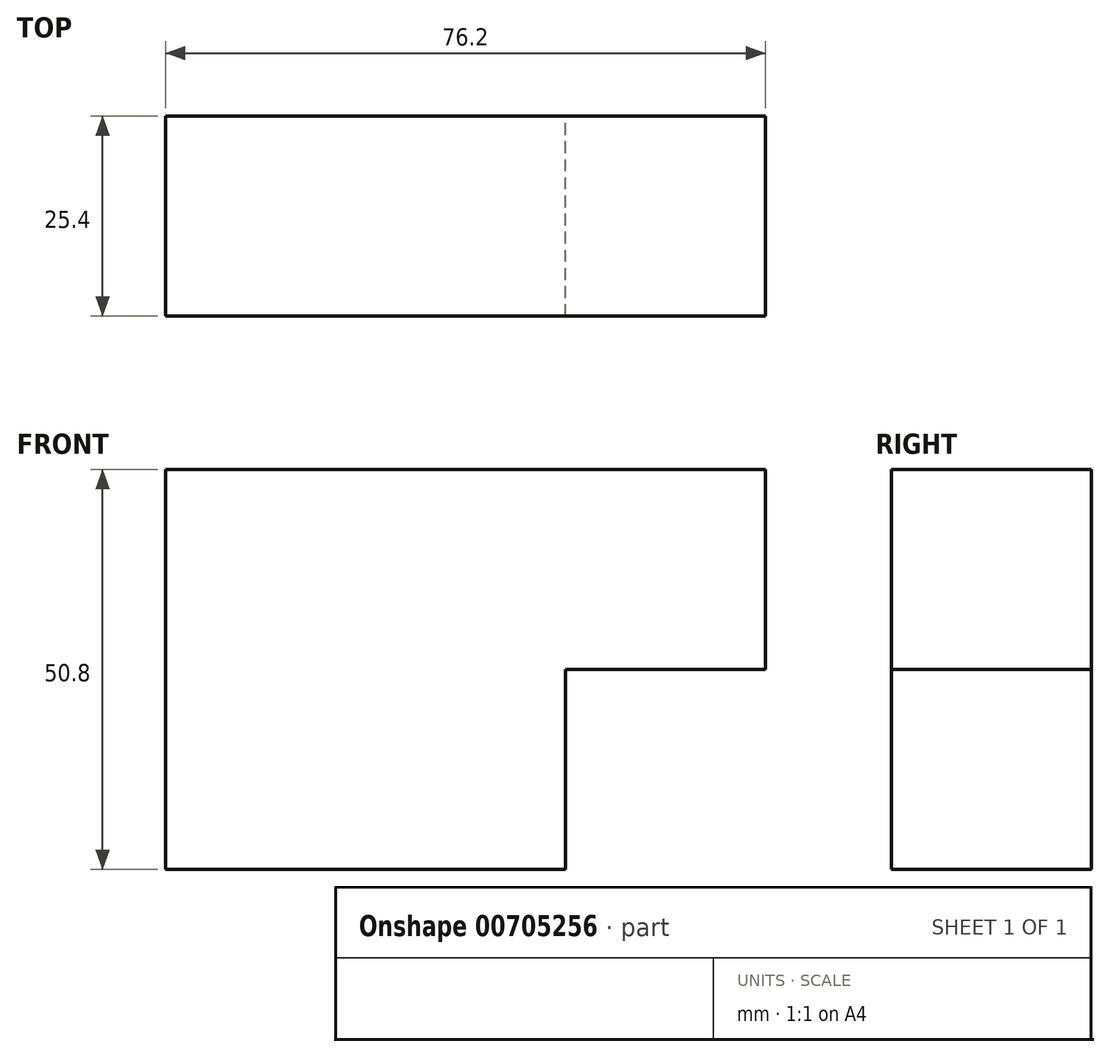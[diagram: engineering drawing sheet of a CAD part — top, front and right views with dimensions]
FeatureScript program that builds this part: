
annotation { "Feature Type Name" : "Feature", "Feature Type Description" : "" }
export const myFeature = defineFeature(function(context is Context, id is Id, definition is map)
    precondition{}
    {
        {
            var Q0;
            Q0=qCreatedBy(makeId("Front.planeOp"),FACE);
            var sketch = newSketch(context, id + "F0", { "sketchPlane" : qUnion([Q0])});
            skLineSegment(sketch, "E0.bottom", {"start": v(0, 0) * mm, "end": v(-25.4, 0) * mm});
            skLineSegment(sketch, "E0.top", {"start": v(0, -25.4) * mm, "end": v(-25.4, -25.4) * mm});
            skLineSegment(sketch, "E0.left", {"start": v(0, 0) * mm, "end": v(0, -25.4) * mm});
            skLineSegment(sketch, "E0.right", {"start": v(-25.4, 0) * mm, "end": v(-25.4, -25.4) * mm});
            skLineSegment(sketch, "E1.bottom", {"start": v(0, 0) * mm, "end": v(25.4, 0) * mm});
            skLineSegment(sketch, "E1.top", {"start": v(0, -25.4) * mm, "end": v(25.4, -25.4) * mm});
            skLineSegment(sketch, "E1.right", {"start": v(25.4, 0) * mm, "end": v(25.4, -25.4) * mm});
            skLineSegment(sketch, "E2.bottom", {"start": v(25.4, 0) * mm, "end": v(50.8, 0) * mm});
            skLineSegment(sketch, "E2.top", {"start": v(25.4, 25.4) * mm, "end": v(50.8, 25.4) * mm});
            skLineSegment(sketch, "E2.left", {"start": v(25.4, 0) * mm, "end": v(25.4, 25.4) * mm});
            skLineSegment(sketch, "E2.right", {"start": v(50.8, 0) * mm, "end": v(50.8, 25.4) * mm});
            skLineSegment(sketch, "E3.bottom", {"start": v(25.4, 25.4) * mm, "end": v(0, 25.4) * mm});
            skLineSegment(sketch, "E3.top", {"start": v(25.4, 0) * mm, "end": v(0, 0) * mm});
            skLineSegment(sketch, "E3.left", {"start": v(25.4, 25.4) * mm, "end": v(25.4, 0) * mm});
            skLineSegment(sketch, "E3.right", {"start": v(0, 25.4) * mm, "end": v(0, 0) * mm});
            skLineSegment(sketch, "E4.bottom", {"start": v(0, 25.4) * mm, "end": v(-25.4, 25.4) * mm});
            skLineSegment(sketch, "E4.right", {"start": v(-25.4, 25.4) * mm, "end": v(-25.4, 0) * mm});
            skSolve(sketch);
        }
        {
            var Q0;
            Q0=makeQuery(id+"F0.imprint","IMPRINT",FACE,{"disambiguationData":[TD([[makeQuery(id+"F0.imprint","IMPRINT",EDGE,{"derivedFrom":sQuery(id+"F0.wireOp",EDGE,"E4.bottom")}),1.0]])]});
            var Q1;
            Q1=makeQuery(id+"F0.imprint","IMPRINT",FACE,{"disambiguationData":[TD([[makeQuery(id+"F0.imprint","IMPRINT",EDGE,{"derivedFrom":sQuery(id+"F0.wireOp",EDGE,"E0.top")}),-1.0]])]});
            var Q2;
            Q2=makeQuery(id+"F0.imprint","IMPRINT",FACE,{"disambiguationData":[TD([[makeQuery(id+"F0.imprint","IMPRINT",EDGE,{"derivedFrom":sQuery(id+"F0.wireOp",EDGE,"E1.top")}),1.0]])]});
            var Q3;
            Q3=makeQuery(id+"F0.imprint","IMPRINT",FACE,{"disambiguationData":[TD([[makeQuery(id+"F0.imprint","IMPRINT",EDGE,{"derivedFrom":sQuery(id+"F0.wireOp",EDGE,"E3.bottom")}),1.0]])]});
            var Q4;
            Q4=makeQuery(id+"F0.imprint","IMPRINT",FACE,{"disambiguationData":[TD([[makeQuery(id+"F0.imprint","IMPRINT",EDGE,{"derivedFrom":sQuery(id+"F0.wireOp",EDGE,"E2.bottom")}),1.0]])]});
            extrude(context, id + "F1", {"entities" : qUnion([Q0, Q1, Q2, Q3, Q4]), "depth" : 25.4 * mm, "offsetDistance" : 25.4 * mm});
        }
    });
